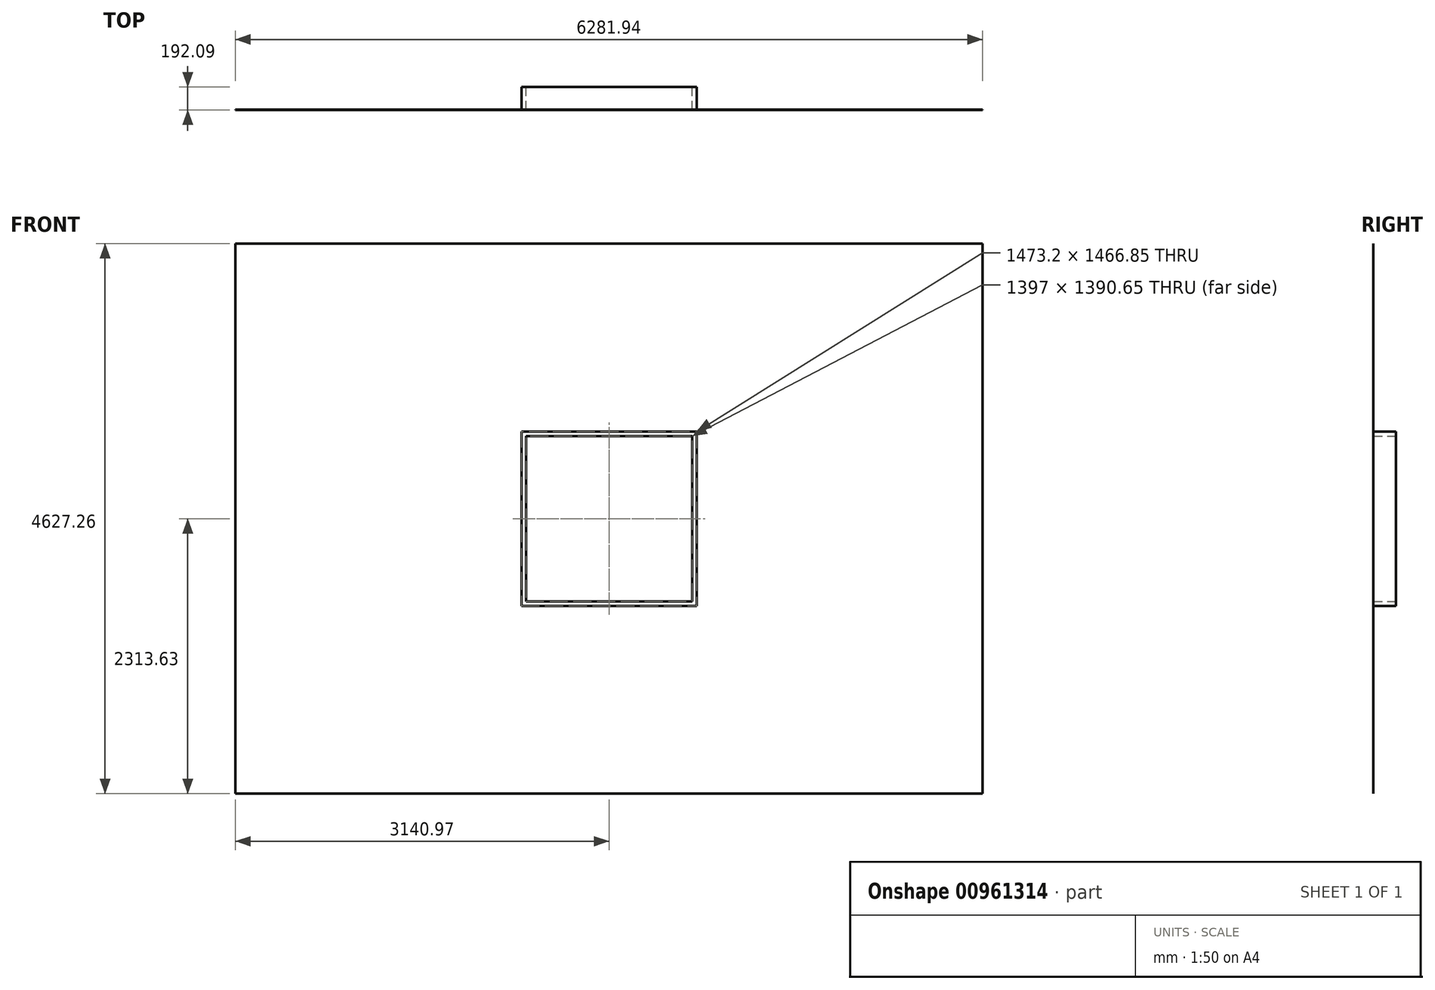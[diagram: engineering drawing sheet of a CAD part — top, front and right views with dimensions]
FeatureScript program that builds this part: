
annotation { "Feature Type Name" : "Feature", "Feature Type Description" : "" }
export const myFeature = defineFeature(function(context is Context, id is Id, definition is map)
    precondition{}
    {
        {
            var Q0;
            Q0=qCreatedBy(makeId("Front.planeOp"),FACE);
            var sketch = newSketch(context, id + "F0", { "sketchPlane" : qUnion([Q0])});
            skLineSegment(sketch, "E0.bottom", {"start": v(698.5, 695.32) * mm, "end": v(-698.5, 695.32) * mm});
            skLineSegment(sketch, "E0.top", {"start": v(698.5, -695.33) * mm, "end": v(-698.5, -695.33) * mm});
            skLineSegment(sketch, "E0.left", {"start": v(698.5, 695.32) * mm, "end": v(698.5, -695.33) * mm});
            skLineSegment(sketch, "E0.right", {"start": v(-698.5, 695.32) * mm, "end": v(-698.5, -695.33) * mm});
            skPoint(sketch, "E0.middle", {"position": v(0, 0) * mm});
            skLineSegment(sketch, "E1.0", {"start": v(736.6, 733.42) * mm, "end": v(736.6, -733.43) * mm});
            skLineSegment(sketch, "E1.1", {"start": v(736.6, 733.42) * mm, "end": v(-736.6, 733.42) * mm});
            skLineSegment(sketch, "E1.2", {"start": v(-736.6, 733.42) * mm, "end": v(-736.6, -733.43) * mm});
            skLineSegment(sketch, "E1.3", {"start": v(736.6, -733.43) * mm, "end": v(-736.6, -733.43) * mm});
            skSolve(sketch);
        }
        {
            var Q0;
            Q0=makeQuery(id+"F0.imprint","IMPRINT",FACE,{"disambiguationData":[TD([[makeQuery(id+"F0.imprint","IMPRINT",EDGE,{"derivedFrom":sQuery(id+"F0.wireOp",EDGE,"E0.bottom")}),-1.0]])]});
            extrude(context, id + "F1", {"entities" : qUnion([Q0]), "depth" : 190.5 * mm, "offsetDistance" : 25.4 * mm});
        }
        {
            var Q0;
            Q0=makeQuery(id+"F1.opExtrude","CAP_FACE",FACE,{"disambiguationData":[OSD([sQuery(id+"F0.wireOp",EDGE,"E0.bottom"),sQuery(id+"F0.wireOp",EDGE,"E0.top"),sQuery(id+"F0.wireOp",EDGE,"E0.left"),sQuery(id+"F0.wireOp",EDGE,"E0.right"),sQuery(id+"F0.wireOp",EDGE,"E1.0"),sQuery(id+"F0.wireOp",EDGE,"E1.1"),sQuery(id+"F0.wireOp",EDGE,"E1.2"),sQuery(id+"F0.wireOp",EDGE,"E1.3")])],"isStart":false});
            var sketch = newSketch(context, id + "F2", { "sketchPlane" : qUnion([Q0])});
            skLineSegment(sketch, "E2.bottom", {"start": v(-736.6, -733.43) * mm, "end": v(736.6, -733.43) * mm});
            skLineSegment(sketch, "E2.top", {"start": v(-736.6, 733.42) * mm, "end": v(736.6, 733.42) * mm});
            skLineSegment(sketch, "E2.left", {"start": v(-736.6, -733.42) * mm, "end": v(-736.6, 733.42) * mm});
            skLineSegment(sketch, "E2.right", {"start": v(736.6, -733.42) * mm, "end": v(736.6, 733.42) * mm});
            skLineSegment(sketch, "E3.bottom", {"start": v(3140.97, 2313.63) * mm, "end": v(-3140.97, 2313.63) * mm});
            skLineSegment(sketch, "E3.top", {"start": v(3140.97, -2313.63) * mm, "end": v(-3140.97, -2313.63) * mm});
            skLineSegment(sketch, "E3.left", {"start": v(3140.97, 2313.63) * mm, "end": v(3140.97, -2313.63) * mm});
            skLineSegment(sketch, "E3.right", {"start": v(-3140.97, 2313.63) * mm, "end": v(-3140.97, -2313.63) * mm});
            skPoint(sketch, "E3.middle", {"position": v(0, 0) * mm});
            skSolve(sketch);
        }
        {
            var Q0;
            Q0=makeQuery(id+"F2.imprint","IMPRINT",FACE,{"disambiguationData":[TD([[makeQuery(id+"F2.imprint","IMPRINT",EDGE,{"derivedFrom":sQuery(id+"F2.wireOp",EDGE,"E2.bottom")}),1.0]])]});
            extrude(context, id + "F3", {"entities" : qUnion([Q0]), "depth" : 1.59 * mm, "offsetDistance" : 25.4 * mm});
        }
    });
